# Revit family: 60-9913-Z5-CM
name_source: partatom
category: Luminarias
revit_build: Autodesk Revit 2017 (Build: 20160225_1515(x64)
units: mm (PartAtom-declared; Revit-internal decimal feet)

## family parameters
Compartido = Sí
Corte con vacíos al cargar = No
Cota de conector redondo = Diámetro de uso
Número OmniClass = 23.80.70.00
Origen de luz = No
Punto de cálculo de habitación = No
Se basa en plano de trabajo = No
Siempre vertical = Sí
Tipo de pieza = Normal
Título OmniClass = Lighting

## types (1)
- 60-9913-Z5-CM
    Acabado = Gris urbano, Semitransparente
    CRI = 80
    Catálogo = Outdoor
    CodigoGubimclass = 50.60.50.20
    CodigoOmniclass = 21-04 50 40
    CodigoUniclass2015 = EF_70_80
    CodigoUniformat2010 = D5040
    DescripcionGubimclass = Iluminación interior
    DescripcionOmniclass = Lighting
    DescripcionUniclass2015 = Lighting
    DescripcionUniformat2010 = Lighting
    EAN13 = 8435381443535
    Eficiencia energética = LED A++
    Etiqueta V/f = 100-240V/50-60Hz
    Fabricante = LEDS C4
    Familia = Proud Symmetrical Head
    FechaVersion = Julio 2020
    Ficha = http://files.leds-c4.com
    Fotometría = http://files.leds-c4.com
    Fuente de luz = 342xLED 40 5450.00 lm
    IK = IK10
    IMC = http://files.leds-c4.com
    IP = IP65
    IfcExportAs = IfcLightFixture
    IfcExportType = NOTDEFINED
    Imagen web = http://files.leds-c4.com
    LDT = http://files.leds-c4.com
    Lumenes reales (lm) = 3110
    Material = Aluminio, Policarbonato
    Peso neto (KG) = 5.94
    Pluma comercial = http://files.leds-c4.com
    Producto descatalogado = Catalogado ES
    Rayo de luz = HORIZONTAL
    Referencia = 60-9913-Z5-CM
    Temperatura color led (K) = Blanco neutro - 4000K
    Tender text (Castellano) = LEDS C4
Proud Symmetrical Head
60-9913-Z5-CM

Cabezal de uso exterior para iluminar hacia abajo. 
Apto para instalar en ambientes con atmósfera marina. Metros cable incluido: 0.4m. Material estructura: Aluminio. Acabado estructura: Gris urbano. Material difusor: Policarbonato. Acabado difusor: Semitransparente. Protección contra los rayos ultravioleta. Garantía: 5 Años. Ta max: 50ºC.

Peso neto del producto (Kg): 5.940
Anchura o diámetro del producto (mm): 440
Altura del producto (mm): 465
Diámetro (mm) admitido del poste en instalación horizontal: 60

Clase 1. IP: IP65. IK: IK10. LED. Nº de portalámparas o Leds: 342. Marca del LED: EDISON. Marca del Driver: SOSEN. Potencia máxima de la fuente de luz: 40W. Temperatura de color: Blanco neutro - 4000K. Índice de reproducción cromática: 80. Steps Mac Adam: 3. Diámetro máximo de la bombilla que admite la luminaria: 50.000h L80B20. UGR:  21.2. Riesgo fotobiológico: RG0. Flujo real (lm): 3110. Flujo nominal (lm): 5450. Lm/W reales: 69. Rango de voltaje/frecuencia: 90-305 VAC. Voltaje: 3. Equipo incluido: Si, electrónico. Equipo multivoltaje incluido. Potencia total: 44.9. Factor de potencia: 0.93.
    Tender text (English) = LEDS C4
Proud Symmetrical Head
60-9913-Z5-CM

Head for outdoor use. 

For downlighting. Suitable for installation in marine environments. Cable meters included: 0.4m. Structure material: Aluminium. Structure finish: Urban grey. Diffuser material: Polycarbonate. Diffuser finish: Semitransparent. UV protection. Warranty: 5 Years. Ta max: 50ºC.

Product net weight (Kg): 5.940
Product width or diameter (mm): 440
Product height (mm): 465
Permitted post diameter (mm) for horizontal installation: 60

Class 1. IP: IP65. IK: IK10. LED. No. of lampholders or LEDs: 342. LED brand: EDISON. Driver brand: SOSEN. Maximum power of light source: 40W. Colour temperature: LED neutral-white 4000K. Colour rendering index: 80. MacAdam Steps: 3. Maximum diameter of luminaire bulb: 50.000h L80B20. UGR:  21.2. Photobiological risk: RG0. Real flux (lm): 3110. Nominal flux (lm): 5450. Lm/Real W: 69. Voltage and frequency range: 90-305 VAC. Voltage: 3. Gear included: Yes, electronic. Multi-voltage gear included. Total power: 44.9. Power factor: 0.93.
    Tipo = Farola
    Vatios (W) = 44.9
    Versión = v1
